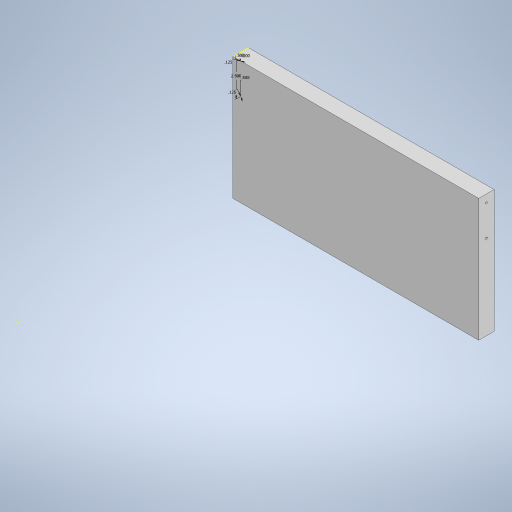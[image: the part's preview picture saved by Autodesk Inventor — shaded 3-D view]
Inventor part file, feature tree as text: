
AUTODESK INVENTOR PART (.ipt)
format: ipt  version: 2023 (Build 270158000, 158)  size: 339,968 bytes
history: native  units: in
note: dims shown in document units (in); Inventor stores cm internally (conversion verified against a paired STEP export)
features: sketch x3, extrude x2
ambient origin geometry x8: Origin, YZ Plane, XZ Plane, XY Plane, X Axis, Y Axis, Z Axis, Center Point
bodies: Solid1 (feature_tree)
feature tree (5):
  extrude  "Extrusion1"  Depth=54.0in
  extrude  "Extrusion2"  Depth=1.0in
  sketch  "Sketch3"  dims[d4=8.0in d5=16.0in d6=8.0in d7=16.0in d8=16.0in d9=8.0in d10=16.0in d11=8.0in d12=4.0in d13=4.0in d14=4.0in d15=4.0in d16=17.0in d17=17.0in d18=17.0in d19=17.0in d20=20.0in d21=1.0in d22=1.0in d23=1.0in d24=1.0in d25=45.0deg d26=2.5in d27=45.0deg d28=45.0deg d29=45.0deg d30=1.0in d31=1.0in d32=1.0in d33=1.0in d34=0.25in d35=0.25in d36=0.25in d37=0.25in d38=0.25in d39=0.25in d40=0.25in d41=0.25in d42=8.0in d43=0.0in d44=0.125in d45=0.125in d46=0.5in d47=0.5in d48=0.5in d49=2.5in d50=1.0in d51=0.0in d52=0.125in d53=0.125in d54=0.5in d55=0.5in d56=0.5in d57=2.5in]
  sketch  "Sketch1"  dims[d0=54.0in d1=54.0in]
  sketch  "Sketch2"  dims[d2=1.0in d3=1.0in]
